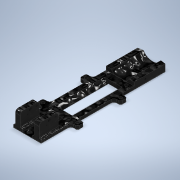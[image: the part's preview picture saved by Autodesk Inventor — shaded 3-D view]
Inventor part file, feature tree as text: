
AUTODESK INVENTOR PART (.ipt)
format: ipt  version: 2020 (Build 240168000, 168)  size: 499,200 bytes
history: native  units: mm
features: sketch x10, projected_geometry x9, extrude x8, fillet x3, hole x2, chamfer x2, plane x1, direct_edit x1, move_body x1
ambient origin geometry x8: Origin, YZ Plane, XZ Plane, XY Plane, X Axis, Y Axis, Z Axis, Center Point
bodies: Solid1 (feature_tree)
feature tree (37):
  extrude  "Extrusion1"  Depth=100.0mm
  plane  "Work Plane1"
  extrude  "Extrusion2"  [1 undecoded]
  extrude  "Extrusion7"  Depth=21.5mm
  extrude  "Extrusion3"  Depth=12.0mm
  hole  "Hole1"  [1 undecoded]
  direct_edit  "Direct Edit1"
  extrude  "Extrusion4"  Depth=5.0mm
  extrude  "Extrusion5"  Depth=5.0mm
  extrude  "Extrusion6"  Depth=2.0mm
  hole  "Hole2"  [1 undecoded]
  extrude  "Extrusion8"  Depth=1.0mm TaperAngle=0.0deg
  fillet  "Fillet1"  Radius=10.5mm
  fillet  "Fillet2"  Radius=31.0mm
  fillet  "Fillet3"  Radius=3.0mm
  chamfer  "Chamfer1"  Distance=5.0mm
  chamfer  "Chamfer2"  Distance=20.0mm
  sketch  "Sketch1"  dims[d0=29.0mm d1=100.0mm]
  sketch  "Sketch2"  dims[d2=4.0mm d3=0.0mm d4=-7.0mm]
  projected_geometry  "Projected Loop1"
  sketch  "Sketch3"  dims[d5=9.5mm d6=21.5mm]
  projected_geometry  "Projected Loop2"
  sketch  "Sketch4"  dims[d7=51.8mm d8=0.0mm d9=12.0mm]
  projected_geometry  "Projected Loop3"
  sketch  "Sketch5"  dims[d10=20.0mm d11=34.0mm d12=0.0mm]
  projected_geometry  "Projected Loop4"
  sketch  "Sketch6"  dims[d13=3.0mm d14=5.0mm]
  projected_geometry  "Projected Loop5"
  sketch  "Sketch7"  dims[d15=3.0mm d16=5.0mm]
  projected_geometry  "Projected Loop6"
  sketch  "Sketch8"  dims[d17=3.1mm d18=6.0mm d19=5.5mm d20=2.0mm d21=90.0deg d22=6.0mm d23=0.0mm d24=5.0mm]
  projected_geometry  "Projected Loop7"
  sketch  "Sketch9"  dims[d25=63.0mm d26=5.0mm]
  projected_geometry  "Projected Loop8"
  sketch  "Sketch10"  dims[d27=63.0mm d28=0.0mm d29=0.0mm d30=31.0mm d31=10.5mm d32=31.0mm d33=3.0mm d34=0.0mm d35=5.0mm d36=20.0mm d37=5.0mm d38=20.0mm d39=14.0mm d40=0.0mm d41=7.0mm d42=7.0mm d43=7.0mm d44=7.0mm d45=4.0mm d46=0.0mm d47=3.5mm d48=3.5mm d49=3.5mm d50=3.5mm d51=3.1mm d52=6.0mm d53=5.5mm d54=2.0mm d55=90.0deg d56=6.0mm d57=0.0mm d58=31.0mm d59=38.0mm d60=34.0mm d61=3.75mm d62=0.0mm d63=55.0mm d64=176.0mm d65=152.0mm d66=85.25mm d67=0.0mm d68=1.0mm d69=3.0mm d70=3.0mm d71=2.0mm d72=1.0mm d73=4.5mm d74=6.0mm d75=45.0deg d76=4.5mm d77=6.0mm d78=45.0deg]
  projected_geometry  "Projected Loop9"
  move_body  "Move1"
note: 3 required parameter values undecoded (feature->parameter linkage not recoverable at this tier; creation-order binding heuristic only, values carry confidence <= 0.55)
